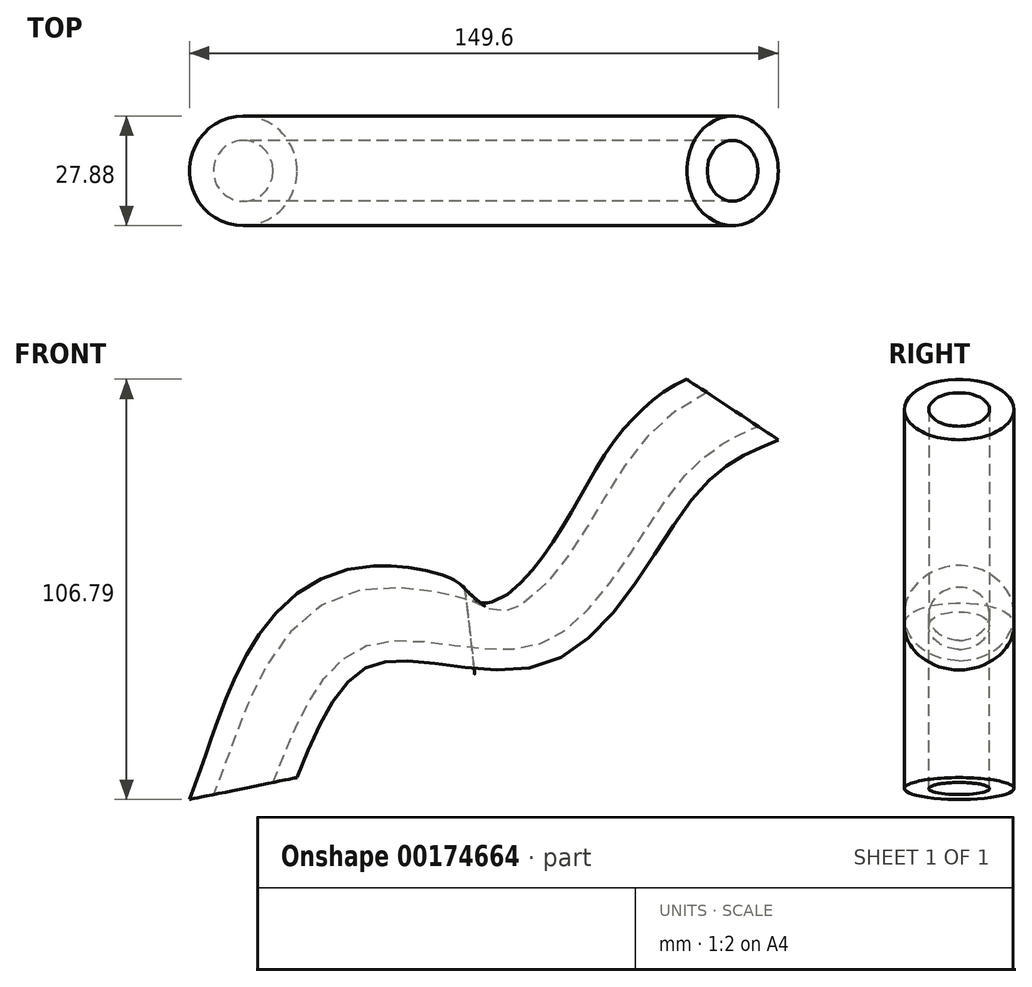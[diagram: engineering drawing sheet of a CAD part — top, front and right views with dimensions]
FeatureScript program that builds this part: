
annotation { "Feature Type Name" : "Feature", "Feature Type Description" : "" }
export const myFeature = defineFeature(function(context is Context, id is Id, definition is map)
    precondition{}
    {
        {
            var Q0;
            Q0=qCreatedBy(makeId("Front.planeOp"),FACE);
            var sketch = newSketch(context, id + "F0", { "sketchPlane" : qUnion([Q0])});
            skFitSpline(sketch, "E0", {"points": [v(-57.02, -21.78) * mm, v(-34.15, 10.8) * mm, v(10.03, 11.44) * mm, v(45.75, 53.1) * mm, v(65.8, 66.9) * mm], "startDerivative": vector(69.08, 174.89) * mm, "endDerivative": vector(102.69, 44.5) * mm});
            skSolve(sketch);
        }
        {
            var Q0;
            Q0=qCreatedBy(makeId("Top.planeOp"),FACE);
            var sketch = newSketch(context, id + "F1", { "sketchPlane" : qUnion([Q0])});
            skCircle(sketch, "E1", {"center": v(-57.02, 0) * mm, "radius": 7.71 * mm});
            skCircle(sketch, "E2", {"center": v(-57.02, 0) * mm, "radius": 13.94 * mm});
            skSolve(sketch);
        }
        {
            var Q0;
            Q0=makeQuery(id+"F1.imprint","IMPRINT",FACE,{"disambiguationData":[TD([[makeQuery(id+"F1.imprint","IMPRINT",EDGE,{"derivedFrom":sQuery(id+"F1.wireOp",EDGE,"E1")}),-1.0]])]});
            var Q1;
            Q1=sQuery(id+"F0.wireOp",EDGE,"E0");
            sweep(context, id + "F2", {"profiles" : qUnion([Q0]), "path" : qUnion([Q1])});
        }
    });
